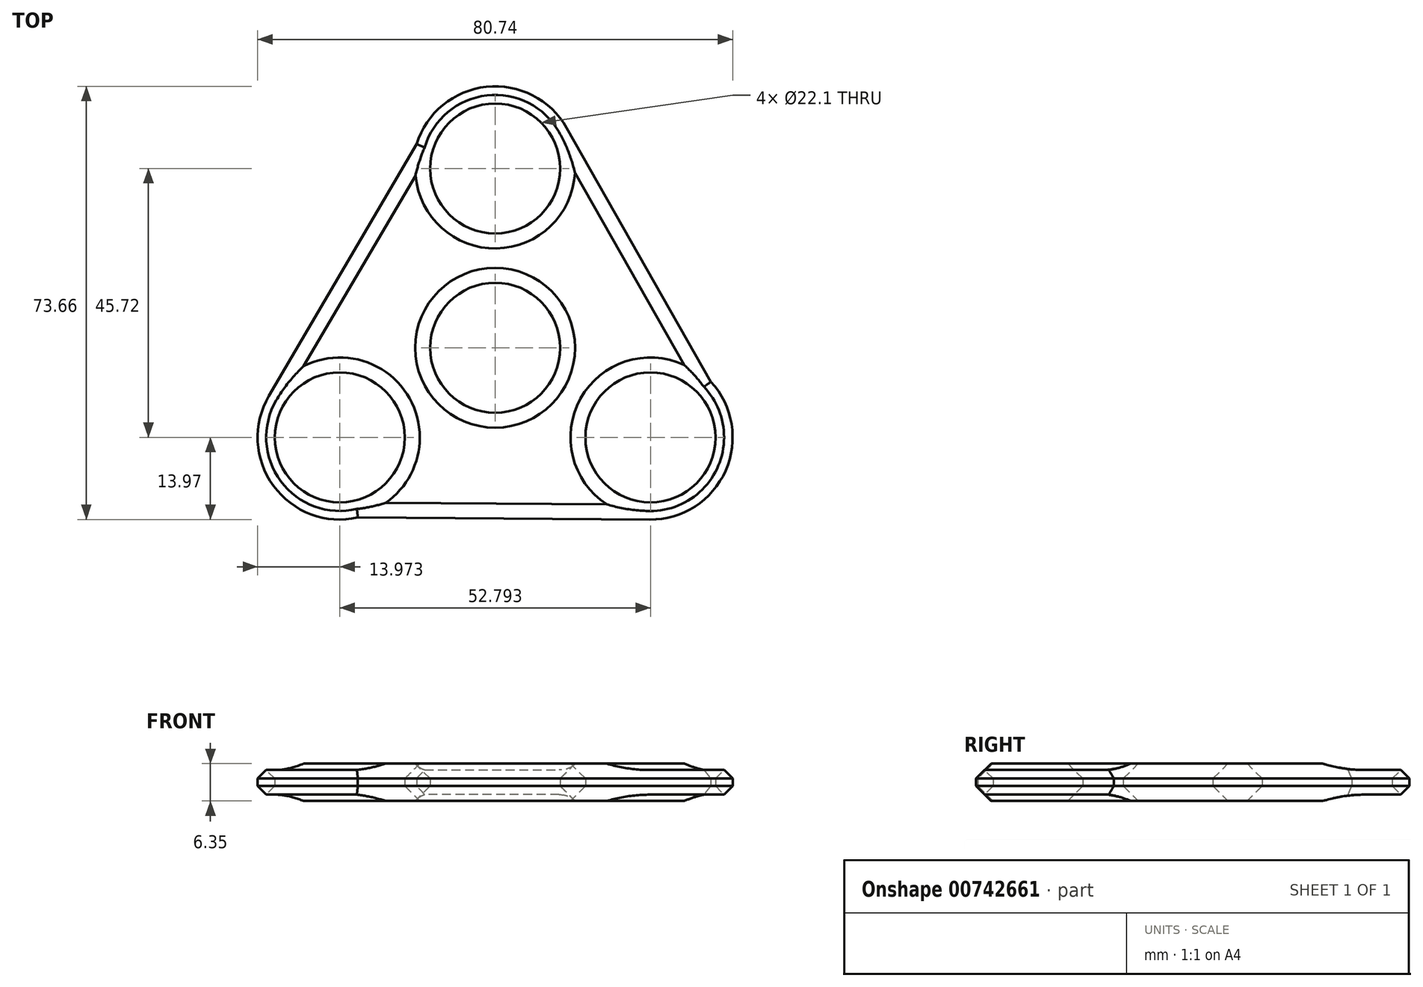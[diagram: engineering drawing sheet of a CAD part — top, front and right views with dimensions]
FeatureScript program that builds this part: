
annotation { "Feature Type Name" : "Feature", "Feature Type Description" : "" }
export const myFeature = defineFeature(function(context is Context, id is Id, definition is map)
    precondition{}
    {
        {
            var Q0;
            Q0=qCreatedBy(makeId("Top.planeOp"),FACE);
            var sketch = newSketch(context, id + "F0", { "sketchPlane" : qUnion([Q0])});
            skCircle(sketch, "E0", {"center": v(0, 0) * mm, "radius": 11.05 * mm});
            skCircle(sketch, "E1", {"center": v(0, 0) * mm, "radius": 13.97 * mm});
            skLineSegment(sketch, "E2", {"start": v(0, 0) * mm, "end": v(0, 30.48) * mm});
            skCircle(sketch, "E3", {"center": v(0, 30.48) * mm, "radius": 11.05 * mm});
            skCircle(sketch, "E4", {"center": v(0, 30.48) * mm, "radius": 13.97 * mm});
            skCircle(sketch, "E5.1.0", {"center": v(-26.4, -15.24) * mm, "radius": 11.05 * mm});
            skCircle(sketch, "E5.1.1", {"center": v(-26.4, -15.24) * mm, "radius": 13.97 * mm});
            skCircle(sketch, "E5.2.0", {"center": v(26.4, -15.24) * mm, "radius": 11.05 * mm});
            skCircle(sketch, "E5.2.1", {"center": v(26.4, -15.24) * mm, "radius": 13.97 * mm});
            skLineSegment(sketch, "E6", {"start": v(-23.33, -28.87) * mm, "end": v(26.3, -29.2) * mm});
            skLineSegment(sketch, "E7.1.0", {"start": v(36.67, -5.77) * mm, "end": v(12.15, 37.38) * mm});
            skLineSegment(sketch, "E7.2.0", {"start": v(-13.34, 34.64) * mm, "end": v(-38.45, -8.17) * mm});
            skSolve(sketch);
        }
        {
            var Q0;
            Q0 = qSketchRegion(id + "F0", true);
            var Q1;
            Q1=makeQuery(id+"F0.imprint","IMPRINT",FACE,{"disambiguationData":[TD([[makeQuery(id+"F0.imprint","IMPRINT",EDGE,{"derivedFrom":sQuery(id+"F0.wireOp",EDGE,"E0")}),-1.0]])]});
            extrude(context, id + "F1", {"entities" : qUnion([Q0, Q1]), "depth" : 6.35 * mm, "offsetDistance" : 25.4 * mm});
        }
        {
            var Q0;
            Q0=makeQuery(id+"F1.opExtrude","CAP_FACE",FACE,{"disambiguationData":[OSD([sQuery(id+"F0.wireOp",EDGE,"E0"),sQuery(id+"F0.wireOp",EDGE,"E3"),sQuery(id+"F0.wireOp",EDGE,"E4"),sQuery(id+"F0.wireOp",EDGE,"E5.1.0"),sQuery(id+"F0.wireOp",EDGE,"E5.1.1"),sQuery(id+"F0.wireOp",EDGE,"E5.2.0"),sQuery(id+"F0.wireOp",EDGE,"E5.2.1"),sQuery(id+"F0.wireOp",EDGE,"E6"),sQuery(id+"F0.wireOp",EDGE,"E7.1.0"),sQuery(id+"F0.wireOp",EDGE,"E7.2.0")])],"isStart":false});
            var Q1;
            Q1=makeQuery(id+"F1.opExtrude","CAP_FACE",FACE,{"disambiguationData":[OSD([sQuery(id+"F0.wireOp",EDGE,"E0"),sQuery(id+"F0.wireOp",EDGE,"E3"),sQuery(id+"F0.wireOp",EDGE,"E4"),sQuery(id+"F0.wireOp",EDGE,"E5.1.0"),sQuery(id+"F0.wireOp",EDGE,"E5.1.1"),sQuery(id+"F0.wireOp",EDGE,"E5.2.0"),sQuery(id+"F0.wireOp",EDGE,"E5.2.1"),sQuery(id+"F0.wireOp",EDGE,"E6"),sQuery(id+"F0.wireOp",EDGE,"E7.1.0"),sQuery(id+"F0.wireOp",EDGE,"E7.2.0")])],"isStart":true});
            chamfer(context, id + "F2", {"entities" : qUnion([Q0, Q1]), "width" : 2.54 * mm, "tangentPropagation" : true});
        }
    });
